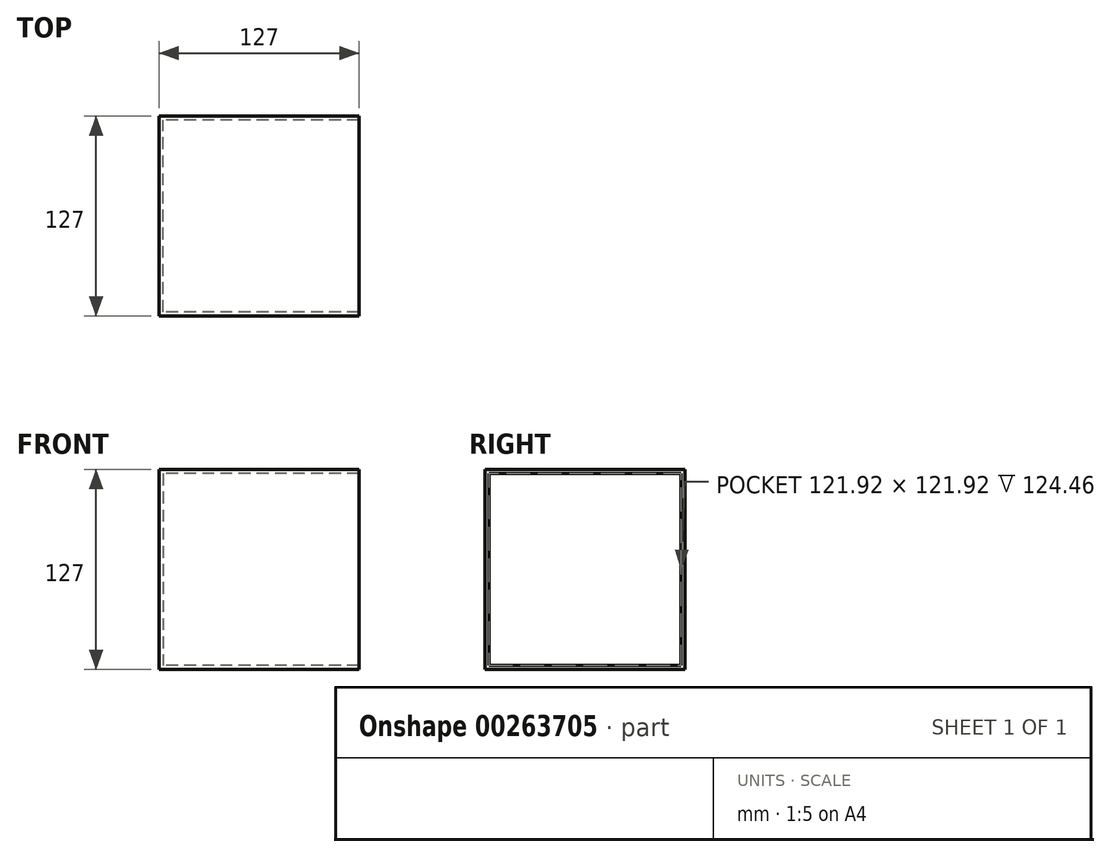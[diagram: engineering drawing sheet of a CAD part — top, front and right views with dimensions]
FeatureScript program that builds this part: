
annotation { "Feature Type Name" : "Feature", "Feature Type Description" : "" }
export const myFeature = defineFeature(function(context is Context, id is Id, definition is map)
    precondition{}
    {
        {
            var Q0;
            Q0=qCreatedBy(makeId("Right.planeOp"),FACE);
            var sketch = newSketch(context, id + "F0", { "sketchPlane" : qUnion([Q0])});
            skLineSegment(sketch, "E0.bottom", {"start": v(-127, 0) * mm, "end": v(0, 0) * mm});
            skLineSegment(sketch, "E0.top", {"start": v(-127, -127) * mm, "end": v(0, -127) * mm});
            skLineSegment(sketch, "E0.left", {"start": v(-127, 0) * mm, "end": v(-127, -127) * mm});
            skLineSegment(sketch, "E0.right", {"start": v(0, 0) * mm, "end": v(0, -127) * mm});
            skSolve(sketch);
        }
        {
            var Q0;
            Q0 = qSketchRegion(id + "F0", true);
            extrude(context, id + "F1", {"entities" : qUnion([Q0]), "depth" : 127 * mm});
        }
        {
            var Q0;
            Q0=makeQuery(id+"F1.opExtrude","CAP_FACE",FACE,{"disambiguationData":[OSD([sQuery(id+"F0.wireOp",EDGE,"E0.bottom"),sQuery(id+"F0.wireOp",EDGE,"E0.top"),sQuery(id+"F0.wireOp",EDGE,"E0.left"),sQuery(id+"F0.wireOp",EDGE,"E0.right")])],"isStart":false});
            var Q1;
            Q1=makeQuery(id+"F1.opExtrude","SWEPT_BODY",BODY,{"disambiguationData":[OSD([sQuery(id+"F0.wireOp",EDGE,"E0.bottom"),sQuery(id+"F0.wireOp",EDGE,"E0.top"),sQuery(id+"F0.wireOp",EDGE,"E0.left"),sQuery(id+"F0.wireOp",EDGE,"E0.right")])]});
            shell(context, id + "F2", {"entities" : qUnion([Q0]), "parts" : qUnion([Q1]), "thickness" : 2.54 * mm});
        }
    });
